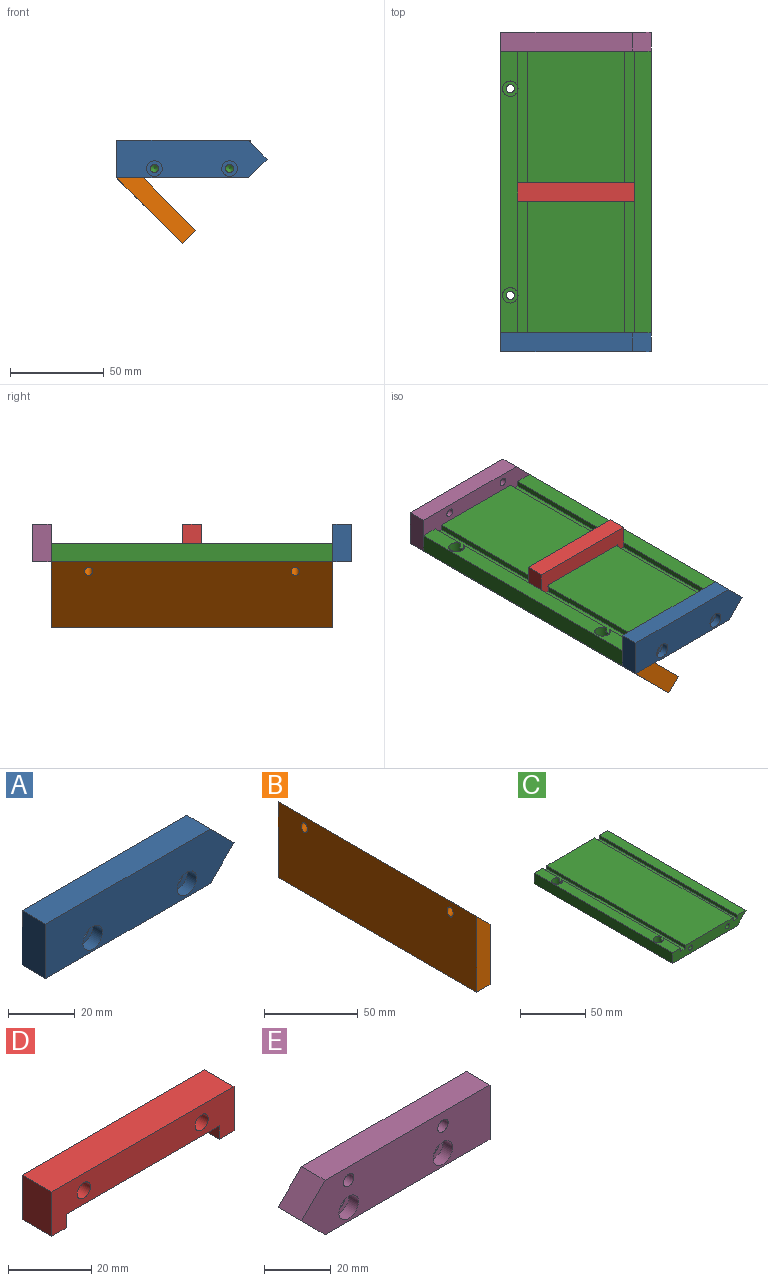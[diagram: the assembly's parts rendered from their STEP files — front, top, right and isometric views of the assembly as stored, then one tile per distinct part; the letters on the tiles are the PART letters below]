
ASSEMBLY  parts=5 mates=4
PART A: 13 faces, bbox 80x10x20 mm
  f0: plane 10x10mm, normal (0.71,0,-0.71), area 141.4mm2, adj f1,f4,f5,f6
  f1: plane 10x10mm, normal (0.71,0,0.71), area 141.4mm2, adj f0,f2,f5,f6
  f2: plane 70x10mm, normal (0,0,1), area 700mm2, adj f1,f3,f5,f6
  f3: plane 20x10mm, normal (-1,0,0), area 200mm2, adj f2,f4,f5,f6
  f4: plane 70x10mm, normal (0,0,-1), area 700mm2, adj f0,f3,f5,f6
  f5: plane 80x20mm, normal (0,-1,0), area 1393.1mm2, adj f0,f1,f2,f3,f4,f9,f12
  f6: plane 80x20mm, normal (0,1,0), area 1469.6mm2, adj f0,f1,f2,f3,f4,f7,f10
  f7: cylinder r=2.2mm len=6mm, axis (0,-1,0), area 82.9mm2, adj f6,f8
  f8: plane 8.25x8.25mm, normal (0,-1,0), area 38.3mm2, adj f7,f9
  f9: cylinder r=4.12mm len=8.25mm, axis (0,-1,0), area 103.7mm2, adj f5,f8
  f10: cylinder r=2.2mm len=6mm, axis (0,-1,0), area 82.9mm2, adj f6,f11
  f11: plane 8.25x8.25mm, normal (0,-1,0), area 38.3mm2, adj f10,f12
  f12: cylinder r=4.12mm len=8.25mm, axis (0,-1,0), area 103.7mm2, adj f5,f11
PART B: 8 faces, bbox 14x150.9x50.4 mm
  f0: plane 150x39.5mm, normal (1,0,0), area 5924.6mm2, adj f1,f3,f4,f5
  f1: plane 150x10mm, normal (0.71,0,0.71), area 2090.9mm2, adj f0,f2,f4,f5,f6,f7
  f2: plane 150.93x50.42mm, normal (-1,0,0), area 7381.6mm2, adj f1,f3,f4,f5,f6,f7
  f3: plane 150x10mm, normal (0,0,-1), area 1500mm2, adj f0,f2,f4,f5
  f4: plane 49.5x10mm, normal (0,-1,0), area 445mm2, adj f0,f1,f2,f3
  f5: plane 49.5x10mm, normal (0,1,0), area 445mm2, adj f0,f1,f2,f3
  f6: cylinder r=2.2mm len=8.2mm, axis (0.71,0,0.71), area 69.1mm2, adj f1,f2
  f7: cylinder r=2.2mm len=8.2mm, axis (0.71,0,0.71), area 69.1mm2, adj f1,f2
PART C: 30 faces, bbox 80x150x10 mm
  f0: plane 150x9mm, normal (0,0,1), area 1243.4mm2, adj f1,f2,f3,f8,f9,f10,f26,f29
  f1: plane 18.99x3mm, normal (1,0,0), area 57mm2, adj f0,f10,f20,f29
  f2: plane 107.98x3mm, normal (1,0,0), area 324mm2, adj f0,f20,f26,f29
  f3: plane 18.99x3mm, normal (1,0,0), area 57mm2, adj f0,f9,f20,f26
  f4: plane 150x52mm, normal (0,0,1), area 7800mm2, adj f9,f10,f19,f21
  f5: plane 150x70mm, normal (0,0,-1), area 10469.6mm2, adj f6,f8,f9,f10,f24,f27
  f6: plane 150x10mm, normal (0.71,0,-0.71), area 2121.3mm2, adj f5,f7,f9,f10
  f7: plane 150x9mm, normal (0,0,1), area 1350mm2, adj f6,f9,f10,f22
  f8: plane 150x10mm, normal (-1,0,0), area 1500mm2, adj f0,f5,f9,f10
  f9: plane 80x10mm, normal (0,-1,0), area 689.6mm2, adj f0,f3,f4,f5,f6,f7,f8,f11
  f10: plane 80x10mm, normal (0,1,0), area 689.6mm2, adj f0,f1,f4,f5,f6,f7,f8,f15
  f11: cylinder r=2.2mm len=12mm, axis (0,-1,0), area 165.9mm2, adj f9,f12
  f12: cone r=0mm half-angle=59deg, axis (0,-1,0), area 17.7mm2, adj f11
  f13: cylinder r=2.2mm len=12mm, axis (0,-1,0), area 165.9mm2, adj f9,f14
  f14: cone r=0mm half-angle=59deg, axis (0,-1,0), area 17.7mm2, adj f13
  f15: cylinder r=2.2mm len=12mm, axis (0,1,0), area 165.9mm2, adj f10,f16
  f16: cone r=0mm half-angle=59deg, axis (0,1,0), area 17.7mm2, adj f15
  f17: cylinder r=2.2mm len=12mm, axis (0,1,0), area 165.9mm2, adj f10,f18
  f18: cone r=0mm half-angle=59deg, axis (0,1,0), area 17.7mm2, adj f17
  f19: plane 150x3mm, normal (-1,0,0), area 450mm2, adj f4,f9,f10,f20
  f20: plane 150x5mm, normal (0,0,1), area 749.7mm2, adj f1,f2,f3,f9,f10,f19,f26,f29
  f21: plane 150x3mm, normal (1,0,0), area 450mm2, adj f4,f9,f10,f23
  f22: plane 150x3mm, normal (-1,0,0), area 450mm2, adj f7,f9,f10,f23
  f23: plane 150x5mm, normal (0,0,1), area 750mm2, adj f9,f10,f21,f22
  f24: cylinder r=2.2mm len=4.4mm, axis (0,0,1), area 41.5mm2, adj f5,f25
  f25: plane 8.25x8.25mm, normal (0,0,1), area 38.3mm2, adj f24,f26
  f26: cylinder r=4.12mm len=8.25mm, axis (0,0,1), area 175.3mm2, adj f0,f2,f3,f20,f25
  f27: cylinder r=2.2mm len=4.4mm, axis (0,0,1), area 41.5mm2, adj f5,f28
  f28: plane 8.25x8.25mm, normal (0,0,1), area 38.3mm2, adj f27,f29
  f29: cylinder r=4.12mm len=8.25mm, axis (0,0,1), area 175.3mm2, adj f0,f1,f2,f20,f28
PART D: 14 faces, bbox 62x10x13 mm
  f0: plane 10x5mm, normal (0,0,-1), area 50mm2, adj f1,f7,f8,f9
  f1: plane 10x4mm, normal (1,0,0), area 40mm2, adj f0,f2,f8,f9
  f2: plane 52x10mm, normal (0,0,-1), area 520mm2, adj f1,f3,f8,f9
  f3: plane 10x4mm, normal (-1,0,0), area 40mm2, adj f2,f4,f8,f9
  f4: plane 10x5mm, normal (0,0,-1), area 50mm2, adj f3,f5,f8,f9
  f5: plane 13x10mm, normal (1,0,0), area 130mm2, adj f4,f6,f8,f9
  f6: plane 62x10mm, normal (0,0,1), area 620mm2, adj f5,f7,f8,f9
  f7: plane 13x10mm, normal (-1,0,0), area 130mm2, adj f0,f6,f8,f9
  f8: plane 62x13mm, normal (0,-1,0), area 566.2mm2, adj f0,f1,f2,f3,f4,f5,f6,f7
  f9: plane 62x13mm, normal (0,1,0), area 598mm2, adj f0,f1,f2,f3,f4,f5,f6,f7
  f10: cylinder r=2.25mm len=4.5mm, axis (0,-1,0), area 56.5mm2, adj f8,f11
  f11: cone r=0mm half-angle=59deg, axis (0,-1,0), area 18.6mm2, adj f10
  f12: cylinder r=2.25mm len=4.5mm, axis (0,-1,0), area 56.5mm2, adj f8,f13
  f13: cone r=0mm half-angle=59deg, axis (0,-1,0), area 18.6mm2, adj f12
PART E: 15 faces, bbox 80x10x20 mm
  f0: plane 10x10mm, normal (-0.71,0,0.71), area 141.4mm2, adj f1,f4,f5,f6
  f1: plane 10x10mm, normal (-0.71,0,-0.71), area 141.4mm2, adj f0,f2,f5,f6
  f2: plane 70x10mm, normal (0,0,-1), area 700mm2, adj f1,f3,f5,f6
  f3: plane 20x10mm, normal (1,0,0), area 200mm2, adj f2,f4,f5,f6
  f4: plane 70x10mm, normal (0,0,1), area 700mm2, adj f0,f3,f5,f6
  f5: plane 80x20mm, normal (0,-1,0), area 1362.7mm2, adj f0,f1,f2,f3,f4,f9,f12,f13
  f6: plane 80x20mm, normal (0,1,0), area 1439.2mm2, adj f0,f1,f2,f3,f4,f7,f10,f13
  f7: cylinder r=2.2mm len=6mm, axis (0,-1,0), area 82.9mm2, adj f6,f8
  f8: plane 8.25x8.25mm, normal (0,-1,0), area 38.3mm2, adj f7,f9
  f9: cylinder r=4.12mm len=8.25mm, axis (0,-1,0), area 103.7mm2, adj f5,f8
  f10: cylinder r=2.2mm len=6mm, axis (0,-1,0), area 82.9mm2, adj f6,f11
  f11: plane 8.25x8.25mm, normal (0,-1,0), area 38.3mm2, adj f10,f12
  f12: cylinder r=4.12mm len=8.25mm, axis (0,-1,0), area 103.7mm2, adj f5,f11
  f13: cylinder r=2.2mm len=10mm, axis (0,-1,0), area 138.2mm2, adj f5,f6
  f14: cylinder r=2.2mm len=10mm, axis (0,-1,0), area 138.2mm2, adj f5,f6
PLACE A t=(-97.36,-187.9,13.9)mm
PLACE B rot(axis=(0,-1,0),45deg) t=(-62.36,-37.9,-21.1)mm
PLACE C t=(-97.36,-37.9,13.9)mm
PLACE D rot(axis=(0,0,-1),180deg) t=(-26.36,-117.9,20.9)mm
PLACE E rot(axis=(0,0,1),180deg) t=(-97.36,-37.9,13.9)mm
MATE fastened C.f13 <-> A.f10  axis (0,-1,0) through (-37.36,-187.9,18.9)mm
MATE fastened C.f13 <-> E.f10  axis (0,1,0) through (-37.36,-37.9,18.9)mm
MATE fastened C.f23 <-> D.f0  axis (0,0,1) through (-28.86,-112.9,20.9)mm
MATE fastened C.f24 <-> B.f6  axis (0,0,-1) through (-92.36,-167.9,13.9)mm
